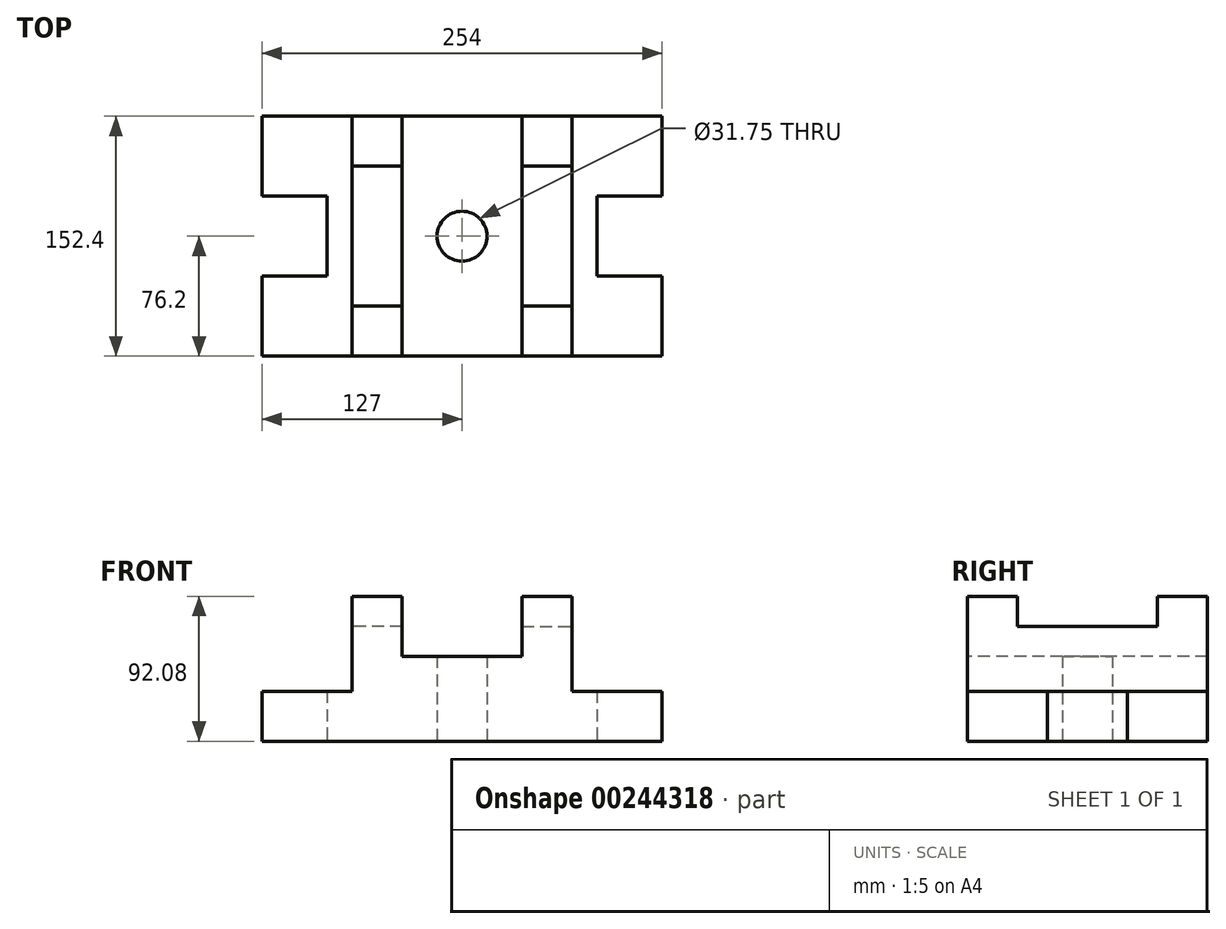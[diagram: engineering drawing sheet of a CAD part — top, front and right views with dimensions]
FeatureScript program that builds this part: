
annotation { "Feature Type Name" : "Feature", "Feature Type Description" : "" }
export const myFeature = defineFeature(function(context is Context, id is Id, definition is map)
    precondition{}
    {
        {
            var Q0;
            Q0=qCreatedBy(makeId("Top.planeOp"),FACE);
            var sketch = newSketch(context, id + "F0", { "sketchPlane" : qUnion([Q0])});
            skCircle(sketch, "E0", {"center": v(0, 0) * mm, "radius": 15.88 * mm});
            skLineSegment(sketch, "E1", {"start": v(0, 0) * mm, "end": v(0, -76.2) * mm});
            skLineSegment(sketch, "E2", {"start": v(85.73, 0) * mm, "end": v(85.73, 25.4) * mm});
            skLineSegment(sketch, "E3", {"start": v(85.73, 0) * mm, "end": v(85.73, -25.4) * mm});
            skLineSegment(sketch, "E4", {"start": v(85.73, 25.4) * mm, "end": v(127, 25.4) * mm});
            skLineSegment(sketch, "E5", {"start": v(85.73, -25.4) * mm, "end": v(127, -25.4) * mm});
            skLineSegment(sketch, "E6", {"start": v(127, 25.4) * mm, "end": v(127, 76.2) * mm});
            skLineSegment(sketch, "E7", {"start": v(127, -25.4) * mm, "end": v(127, -76.2) * mm});
            skLineSegment(sketch, "E8", {"start": v(0, 76.2) * mm, "end": v(127, 76.2) * mm});
            skLineSegment(sketch, "E9", {"start": v(0, -76.2) * mm, "end": v(127, -76.2) * mm});
            skLineSegment(sketch, "E10", {"start": v(0, 76.2) * mm, "end": v(0, 0) * mm});
            skLineSegment(sketch, "E11", {"start": v(69.85, 76.2) * mm, "end": v(69.85, -76.2) * mm});
            skLineSegment(sketch, "E12", {"start": v(38.1, 76.2) * mm, "end": v(38.1, -76.2) * mm});
            skLineSegment(sketch, "E13", {"start": v(38.1, 44.45) * mm, "end": v(69.85, 44.45) * mm});
            skLineSegment(sketch, "E14", {"start": v(38.1, -44.45) * mm, "end": v(69.85, -44.45) * mm});
            skLineSegment(sketch, "E15.MirrorCS", {"start": v(0, 76.2) * mm, "end": v(-127, 76.2) * mm});
            skLineSegment(sketch, "E16.MirrorCS", {"start": v(-85.73, 0) * mm, "end": v(-85.73, 25.4) * mm});
            skLineSegment(sketch, "E17.MirrorCS", {"start": v(-69.85, 76.2) * mm, "end": v(-69.85, -76.2) * mm});
            skLineSegment(sketch, "E18.MirrorCS", {"start": v(-38.1, 76.2) * mm, "end": v(-38.1, -76.2) * mm});
            skLineSegment(sketch, "E19.MirrorCS", {"start": v(-38.1, 44.45) * mm, "end": v(-69.85, 44.45) * mm});
            skLineSegment(sketch, "E20.MirrorCS", {"start": v(-127, 25.4) * mm, "end": v(-127, 76.2) * mm});
            skLineSegment(sketch, "E21.MirrorCS", {"start": v(-85.72, 25.4) * mm, "end": v(-127, 25.4) * mm});
            skLineSegment(sketch, "E22.MirrorCS", {"start": v(-85.73, 0) * mm, "end": v(-85.73, -25.4) * mm});
            skLineSegment(sketch, "E23.MirrorCS", {"start": v(-85.73, -25.4) * mm, "end": v(-127, -25.4) * mm});
            skLineSegment(sketch, "E24.MirrorCS", {"start": v(-127, -25.4) * mm, "end": v(-127, -76.2) * mm});
            skLineSegment(sketch, "E25.MirrorCS", {"start": v(0, -76.2) * mm, "end": v(-127, -76.2) * mm});
            skLineSegment(sketch, "E26.MirrorCS", {"start": v(-38.1, -44.45) * mm, "end": v(-69.85, -44.45) * mm});
            skSolve(sketch);
        }
        {
            var Q0;
            Q0=makeQuery(id+"F0.imprint","IMPRINT",FACE,{"disambiguationData":[TD([[makeQuery(id+"F0.imprint","IMPRINT",EDGE,{"derivedFrom":sQuery(id+"F0.wireOp",EDGE,"E16.MirrorCS")}),-1.0]])]});
            var Q1;
            Q1=makeQuery(id+"F0.imprint","IMPRINT",FACE,{"disambiguationData":[TD([[makeQuery(id+"F0.imprint","IMPRINT",EDGE,{"derivedFrom":sQuery(id+"F0.wireOp",EDGE,"E2")}),1.0]])]});
            extrude(context, id + "F1", {"entities" : qUnion([Q0, Q1]), "depth" : 31.75 * mm});
        }
        {
            var Q0;
            {var subQ5=sQuery(id+"F0.wireOp",EDGE,"E19.MirrorCS");Q0=makeQuery(id+"F0.imprint","IMPRINT",FACE,{"disambiguationData":[TD([[makeQuery(id+"F0.imprint","IMPRINT",EDGE,{"derivedFrom":subQ5}),-1.0]])]});}
            var Q1;
            {var subQ3=sQuery(id+"F0.wireOp",EDGE,"E26.MirrorCS");Q1=makeQuery(id+"F0.imprint","IMPRINT",FACE,{"disambiguationData":[TD([[makeQuery(id+"F0.imprint","IMPRINT",EDGE,{"derivedFrom":subQ3}),1.0]])]});}
            var Q2;
            {var subQ5=sQuery(id+"F0.wireOp",EDGE,"E13");Q2=makeQuery(id+"F0.imprint","IMPRINT",FACE,{"disambiguationData":[TD([[makeQuery(id+"F0.imprint","IMPRINT",EDGE,{"derivedFrom":subQ5}),1.0]])]});}
            var Q3;
            {var subQ5=sQuery(id+"F0.wireOp",EDGE,"E14");Q3=makeQuery(id+"F0.imprint","IMPRINT",FACE,{"disambiguationData":[TD([[makeQuery(id+"F0.imprint","IMPRINT",EDGE,{"derivedFrom":subQ5}),-1.0]])]});}
            extrude(context, id + "F2", {"entities" : qUnion([Q0, Q1, Q2, Q3]), "operationType" : NewBodyOperationType.ADD, "depth" : 92.07 * mm});
        }
        {
            var Q0;
            {var subQ5=sQuery(id+"F0.wireOp",EDGE,"E0");var subQ10=sQuery(id+"F0.wireOp",EDGE,"E1");var subQ12=makeQuery(id+"F0.imprint","INTERSECT",VERTEX,{"derivedFrom":[subQ5,subQ10]});Q0=makeQuery(id+"F0.imprint","IMPRINT",FACE,{"disambiguationData":[TD([[makeQuery(id+"F0.imprint","IMPRINT",EDGE,{"disambiguationData":[TD([[subQ12,1.0]])],"derivedFrom":subQ5}),-1.0]])]});}
            var Q1;
            {var subQ1=sQuery(id+"F0.wireOp",EDGE,"E1");var subQ9=sQuery(id+"F0.wireOp",EDGE,"E0");var subQ10=makeQuery(id+"F0.imprint","INTERSECT",VERTEX,{"derivedFrom":[subQ9,subQ1]});Q1=makeQuery(id+"F0.imprint","IMPRINT",FACE,{"disambiguationData":[TD([[makeQuery(id+"F0.imprint","IMPRINT",EDGE,{"disambiguationData":[TD([[subQ10,-1.0]])],"derivedFrom":subQ9}),-1.0]])]});}
            extrude(context, id + "F3", {"entities" : qUnion([Q0, Q1]), "operationType" : NewBodyOperationType.ADD, "depth" : 53.97 * mm});
        }
        {
            var Q0;
            {var subQ0=sQuery(id+"F0.wireOp",EDGE,"E19.MirrorCS");Q0=makeQuery(id+"F0.imprint","IMPRINT",FACE,{"disambiguationData":[TD([[makeQuery(id+"F0.imprint","IMPRINT",EDGE,{"derivedFrom":subQ0}),1.0]])]});}
            var Q1;
            {var subQ0=sQuery(id+"F0.wireOp",EDGE,"E13");Q1=makeQuery(id+"F0.imprint","IMPRINT",FACE,{"disambiguationData":[TD([[makeQuery(id+"F0.imprint","IMPRINT",EDGE,{"derivedFrom":subQ0}),-1.0]])]});}
            extrude(context, id + "F4", {"entities" : qUnion([Q0, Q1]), "operationType" : NewBodyOperationType.ADD, "depth" : 73.02 * mm});
        }
        {
            var Q0;
            Q0=makeQuery(id+"F0.imprint","IMPRINT",FACE,{"disambiguationData":[TD([[makeQuery(id+"F0.imprint","IMPRINT",EDGE,{"derivedFrom":sQuery(id+"F0.wireOp",EDGE,"E16.MirrorCS")}),-1.0]])]});
            var Q1;
            Q1=makeQuery(id+"F0.imprint","IMPRINT",FACE,{"disambiguationData":[TD([[makeQuery(id+"F0.imprint","IMPRINT",EDGE,{"derivedFrom":sQuery(id+"F0.wireOp",EDGE,"E2")}),1.0]])]});
            extrude(context, id + "F5", {"entities" : qUnion([Q0, Q1]), "operationType" : NewBodyOperationType.ADD, "depth" : 31.75 * mm});
        }
    });
